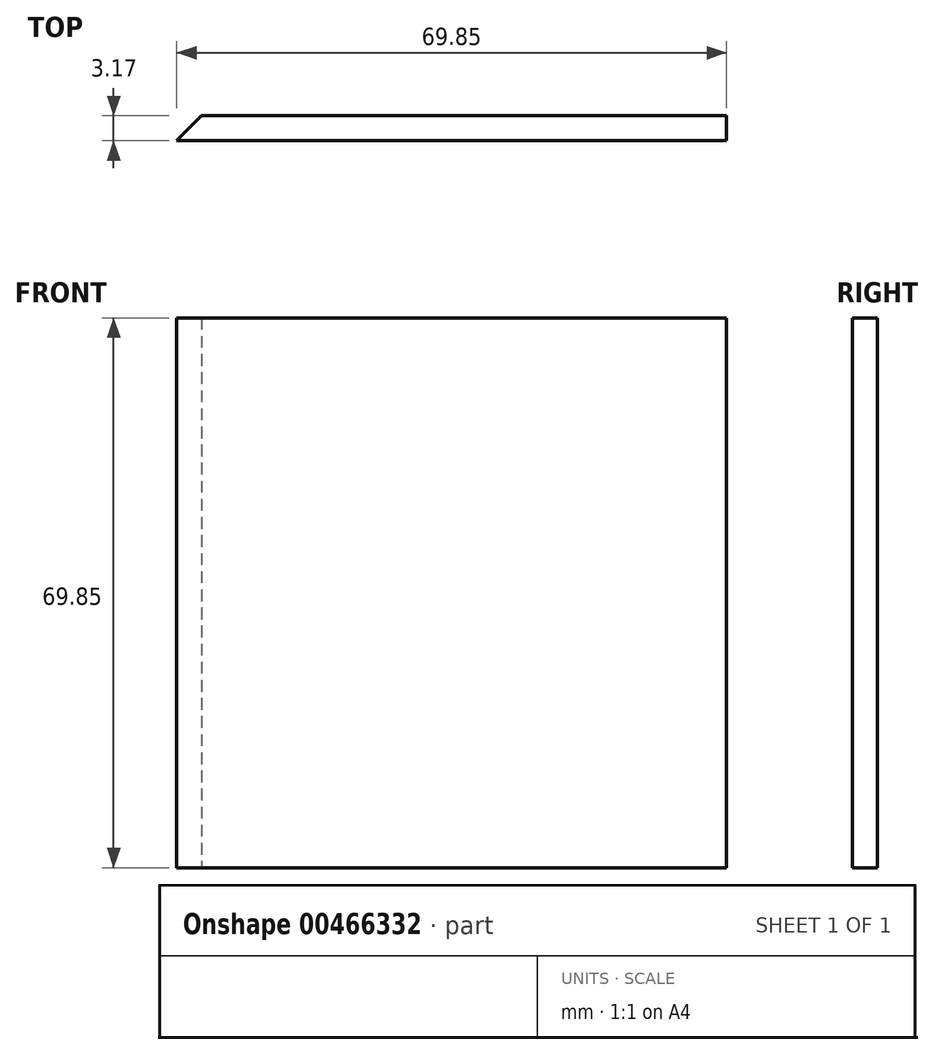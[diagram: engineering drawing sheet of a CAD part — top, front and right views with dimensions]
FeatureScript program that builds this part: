
annotation { "Feature Type Name" : "Feature", "Feature Type Description" : "" }
export const myFeature = defineFeature(function(context is Context, id is Id, definition is map)
    precondition{}
    {
        {
            var Q0;
            Q0=qCreatedBy(makeId("Top.planeOp"),FACE);
            var sketch = newSketch(context, id + "F0", { "sketchPlane" : qUnion([Q0])});
            skLineSegment(sketch, "E0", {"start": v(-44.97, 5.1) * mm, "end": v(-41.8, 8.28) * mm});
            skLineSegment(sketch, "E1", {"start": v(-41.8, 8.28) * mm, "end": v(24.88, 8.28) * mm});
            skLineSegment(sketch, "E2", {"start": v(24.88, 8.28) * mm, "end": v(24.88, 5.1) * mm});
            skLineSegment(sketch, "E3", {"start": v(-44.97, 5.1) * mm, "end": v(24.88, 5.1) * mm});
            skSolve(sketch);
        }
        {
            var Q0;
            Q0=qSketchRegion(id+"F0",true);
            extrude(context, id + "F1", {"entities" : qUnion([Q0]), "depth" : 69.85 * mm});
        }
    });
